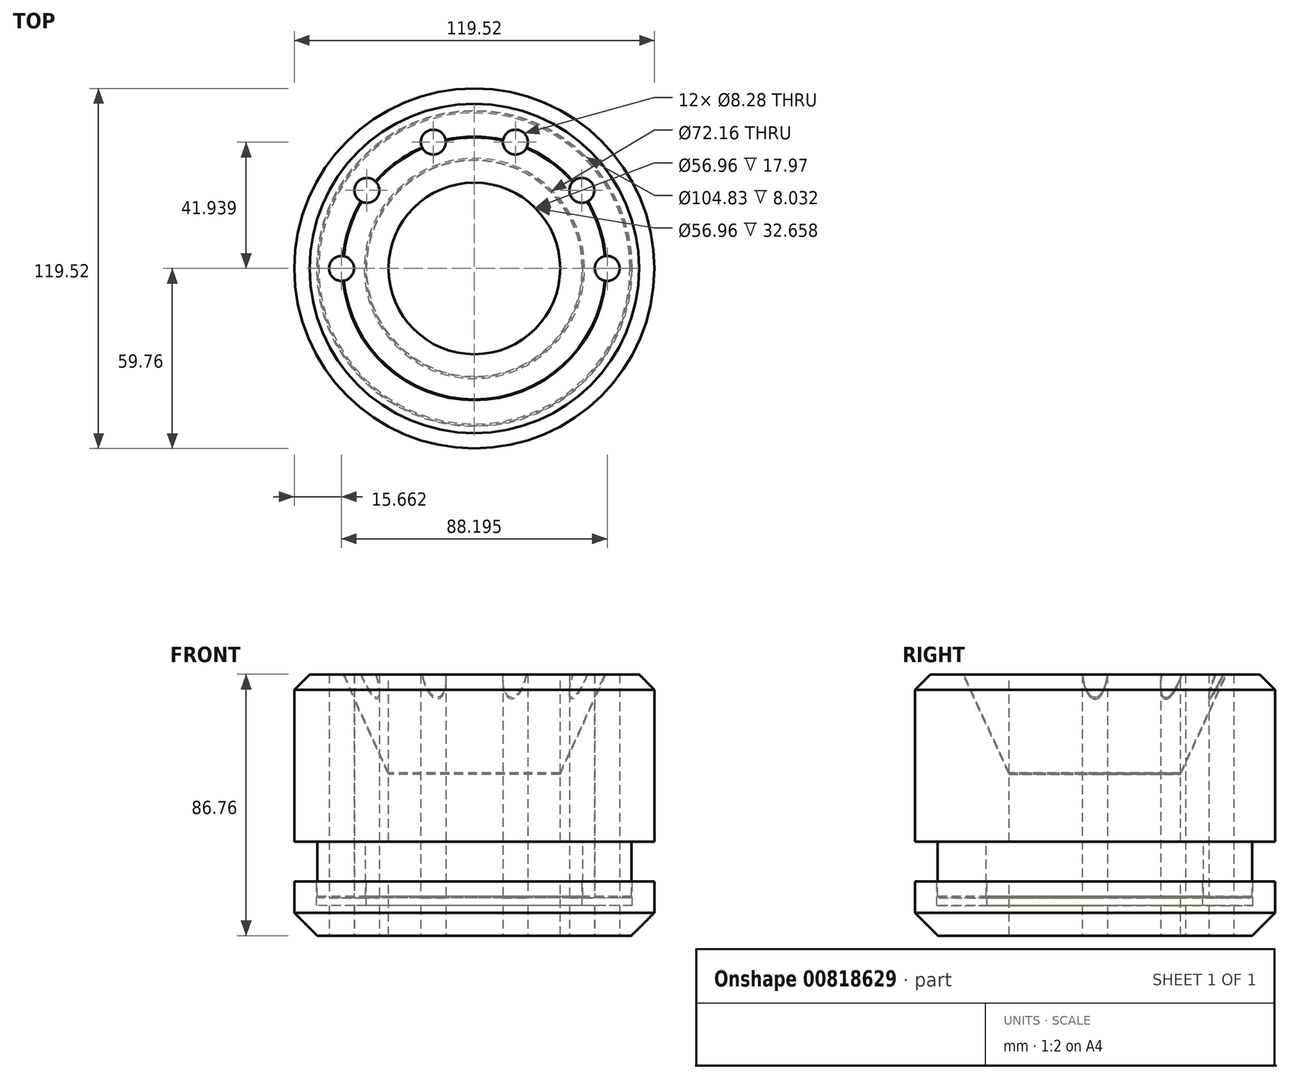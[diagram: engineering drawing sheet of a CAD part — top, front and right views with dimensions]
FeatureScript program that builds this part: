
annotation { "Feature Type Name" : "Feature", "Feature Type Description" : "" }
export const myFeature = defineFeature(function(context is Context, id is Id, definition is map)
    precondition{}
    {
        {
            var Q0;
            Q0=qCreatedBy(makeId("Front.planeOp"),FACE);
            var sketch = newSketch(context, id + "F0", { "sketchPlane" : qUnion([Q0])});
            skLineSegment(sketch, "E0.bottom", {"start": v(-28.48, 14.74) * mm, "end": v(-36.08, 14.74) * mm});
            skLineSegment(sketch, "E0.top", {"start": v(-28.48, 24.8) * mm, "end": v(-59.76, 24.8) * mm});
            skLineSegment(sketch, "E0.left", {"start": v(-28.48, 14.74) * mm, "end": v(-28.48, 24.8) * mm});
            skLineSegment(sketch, "E0.right", {"start": v(-59.76, 14.74) * mm, "end": v(-59.76, 24.8) * mm});
            skPoint(sketch, "E0.middle", {"position": v(-44.12, 19.77) * mm});
            skLineSegment(sketch, "E1.bottom", {"start": v(-36.08, -3.98) * mm, "end": v(-52.16, -3.98) * mm});
            skLineSegment(sketch, "E1.left", {"start": v(-36.08, -3.98) * mm, "end": v(-36.08, 14.74) * mm});
            skLineSegment(sketch, "E1.right", {"start": v(-52.16, -3.98) * mm, "end": v(-52.16, 14.74) * mm});
            skPoint(sketch, "E1.middle", {"position": v(-44.12, 5.33) * mm});
            skLineSegment(sketch, "E2.trimOffspring", {"start": v(-52.16, 14.74) * mm, "end": v(-59.76, 14.74) * mm});
            skLineSegment(sketch, "E3.bottom", {"start": v(-28.48, 1.52) * mm, "end": v(-35.82, 1.52) * mm});
            skLineSegment(sketch, "E3.top", {"start": v(-28.48, -16.45) * mm, "end": v(-59.76, -16.45) * mm});
            skLineSegment(sketch, "E3.left", {"start": v(-28.48, 1.52) * mm, "end": v(-28.48, -16.45) * mm});
            skLineSegment(sketch, "E3.right", {"start": v(-59.76, 1.52) * mm, "end": v(-59.76, -16.45) * mm});
            skPoint(sketch, "E3.middle", {"position": v(-44.12, -7.47) * mm});
            skPoint(sketch, "E3.middle.positionSnap0", {"position": v(-44.12, -3.98) * mm});
            skPoint(sketch, "E3.centerSnap0", {"position": v(-44.12, -3.98) * mm});
            skLineSegment(sketch, "E4.0", {"start": v(-52.41, -6.52) * mm, "end": v(-52.41, 1.52) * mm});
            skLineSegment(sketch, "E5.0", {"start": v(-35.82, -6.52) * mm, "end": v(-35.82, 1.52) * mm});
            skLineSegment(sketch, "E6.0", {"start": v(-35.82, -6.52) * mm, "end": v(-52.41, -6.52) * mm});
            skLineSegment(sketch, "E7.trimOffspring", {"start": v(-52.41, 1.52) * mm, "end": v(-59.76, 1.52) * mm});
            skLineSegment(sketch, "E8", {"start": v(0, 57.13) * mm, "end": v(0, -56.52) * mm, "construction": true});
            skLineSegment(sketch, "E9.top", {"start": v(-28.48, 70.3) * mm, "end": v(-43.48, 70.3) * mm});
            skLineSegment(sketch, "E9.left", {"start": v(-28.48, 24.8) * mm, "end": v(-28.48, 37.04) * mm});
            skLineSegment(sketch, "E9.right", {"start": v(-59.76, 24.8) * mm, "end": v(-59.76, 70.3) * mm});
            skPoint(sketch, "E9.middle", {"position": v(-44.12, 47.55) * mm});
            skLineSegment(sketch, "E10", {"start": v(-43.76, 70.3) * mm, "end": v(-28.48, 37.04) * mm});
            skLineSegment(sketch, "E11.0", {"start": v(-43.48, 70.3) * mm, "end": v(-28.48, 37.65) * mm});
            skLineSegment(sketch, "E12.trimOffspring", {"start": v(-43.76, 70.3) * mm, "end": v(-59.76, 70.3) * mm});
            skLineSegment(sketch, "E13.trimOffspring", {"start": v(-28.48, 37.65) * mm, "end": v(-28.48, 70.3) * mm});
            skSolve(sketch);
        }
        {
            var Q0;
            Q0=makeQuery(id+"F0.imprint","IMPRINT",FACE,{"disambiguationData":[TD([[makeQuery(id+"F0.imprint","IMPRINT",EDGE,{"derivedFrom":sQuery(id+"F0.wireOp",EDGE,"E0.bottom")}),-1.0]])]});
            var Q1;
            Q1=makeQuery(id+"F0.imprint","IMPRINT",FACE,{"disambiguationData":[TD([[makeQuery(id+"F0.imprint","IMPRINT",EDGE,{"derivedFrom":sQuery(id+"F0.wireOp",EDGE,"E3.bottom")}),1.0]])]});
            var Q2;
            Q2=makeQuery(id+"F0.imprint","IMPRINT",FACE,{"disambiguationData":[TD([[makeQuery(id+"F0.imprint","IMPRINT",EDGE,{"derivedFrom":sQuery(id+"F0.wireOp",EDGE,"E0.top")}),-1.0]])]});
            var Q3;
            Q3=makeQuery(id+"F0.imprint","IMPRINT",FACE,{"disambiguationData":[TD([[makeQuery(id+"F0.imprint","IMPRINT",EDGE,{"derivedFrom":sQuery(id+"F0.wireOp",EDGE,"E9.top")}),1.0]])]});
            var Q4;
            Q4=sQuery(id+"F0.wireOp",EDGE,"E8");
            revolve(context, id + "F1", {"surfaceOperationType" : NewSurfaceOperationType.NEW, "entities" : qUnion([Q0, Q1, Q2, Q3]), "axis" : qUnion([Q4]), "revolveType" : RevolveType.FULL});
        }
        {
            var Q0;
            Q0=makeQuery(id+"F1.opRevolve","SWEPT_EDGE",EDGE,{"disambiguationData":[OSD([sQuery(id+"F0.wireOp",EDGE,"E3.top"),sQuery(id+"F0.wireOp",EDGE,"E3.right")])]});
            chamfer(context, id + "F2", {"entities" : qUnion([Q0]), "width" : 7.62 * mm, "tangentPropagation" : true});
        }
        {
            var Q0;
            Q0=makeQuery(id+"F1.opRevolve","SWEPT_FACE",FACE,{"disambiguationData":[OSD([sQuery(id+"F0.wireOp",EDGE,"E3.top")])]});
            var sketch = newSketch(context, id + "F3", { "sketchPlane" : qUnion([Q0])});
            skCircle(sketch, "E14", {"center": v(0, 0) * mm, "radius": 44.1 * mm, "construction": true});
            skCircle(sketch, "E15", {"center": v(-44.1, 0) * mm, "radius": 4.14 * mm});
            skCircle(sketch, "E16.1.0", {"center": v(-35.68, -25.92) * mm, "radius": 4.14 * mm});
            skCircle(sketch, "E16.2.0", {"center": v(-13.63, -41.94) * mm, "radius": 4.14 * mm});
            skCircle(sketch, "E16.3.0", {"center": v(13.63, -41.94) * mm, "radius": 4.14 * mm});
            skCircle(sketch, "E16.4.0", {"center": v(35.68, -25.92) * mm, "radius": 4.14 * mm});
            skCircle(sketch, "E16.5.0", {"center": v(44.1, 0) * mm, "radius": 4.14 * mm});
            skLineSegment(sketch, "E16.anchor1", {"start": v(0, 0) * mm, "end": v(-44.1, 0) * mm, "construction": true});
            skLineSegment(sketch, "E16.anchor2", {"start": v(0, 0) * mm, "end": v(44.1, 0) * mm, "construction": true});
            skSolve(sketch);
        }
        {
            var Q0;
            Q0 = qSketchRegion(id + "F3", true);
            extrude(context, id + "F4", {"entities" : qUnion([Q0]), "operationType" : NewBodyOperationType.REMOVE, "endBound" : BoundingType.THROUGH_ALL, "oppositeDirection" : true, "depth" : 25.4 * mm, "offsetDistance" : 25.4 * mm});
        }
        {
            var Q0;
            Q0=makeQuery(id+"F1.opRevolve","SWEPT_FACE",FACE,{"disambiguationData":[OSD([sQuery(id+"F0.wireOp",EDGE,"E1.bottom")])]});
            var sketch = newSketch(context, id + "F5", { "sketchPlane" : qUnion([Q0])});
            skCircle(sketch, "E17", {"center": v(0, 0) * mm, "radius": 44.1 * mm, "construction": true});
            skCircle(sketch, "E18", {"center": v(-44.1, 0) * mm, "radius": 4.14 * mm});
            skCircle(sketch, "E19.1.0", {"center": v(-35.68, -25.92) * mm, "radius": 4.14 * mm});
            skCircle(sketch, "E19.2.0", {"center": v(-13.63, -41.94) * mm, "radius": 4.14 * mm});
            skCircle(sketch, "E19.3.0", {"center": v(13.63, -41.94) * mm, "radius": 4.14 * mm});
            skCircle(sketch, "E19.4.0", {"center": v(35.68, -25.92) * mm, "radius": 4.14 * mm});
            skCircle(sketch, "E19.5.0", {"center": v(44.1, 0) * mm, "radius": 4.14 * mm});
            skLineSegment(sketch, "E19.anchor1", {"start": v(0, 0) * mm, "end": v(-44.1, 0) * mm, "construction": true});
            skLineSegment(sketch, "E19.anchor2", {"start": v(0, 0) * mm, "end": v(44.1, 0) * mm, "construction": true});
            skSolve(sketch);
        }
        {
            var Q0;
            Q0 = qSketchRegion(id + "F5", true);
            extrude(context, id + "F6", {"entities" : qUnion([Q0]), "operationType" : NewBodyOperationType.REMOVE, "oppositeDirection" : true, "depth" : 19.05 * mm, "offsetDistance" : 25.4 * mm});
        }
        {
            var Q0;
            Q0=makeQuery(id+"F1.opRevolve","SWEPT_EDGE",EDGE,{"disambiguationData":[OSD([sQuery(id+"F0.wireOp",EDGE,"E1.bottom"),sQuery(id+"F0.wireOp",EDGE,"E1.right")])]});
            var Q1;
            Q1=makeQuery(id+"F6.boolean.opBoolean","COPY",EDGE,{"derivedFrom":makeQuery(id+"F6.opExtrude","CAP_EDGE",EDGE,{"disambiguationData":[OSD([sQuery(id+"F5.wireOp",EDGE,"E18")])],"isStart":true})});
            var Q2;
            Q2=makeQuery(id+"F1.opRevolve","SWEPT_EDGE",EDGE,{"disambiguationData":[OSD([sQuery(id+"F0.wireOp",EDGE,"E1.bottom"),sQuery(id+"F0.wireOp",EDGE,"E1.left")])]});
            chamfer(context, id + "F7", {"entities" : qUnion([Q0, Q1, Q2]), "width" : 0.5 * mm, "tangentPropagation" : true});
        }
        {
            var Q0;
            Q0=makeQuery(id+"F1.opRevolve","SWEPT_EDGE",EDGE,{"disambiguationData":[OSD([sQuery(id+"F0.wireOp",EDGE,"E1.right"),sQuery(id+"F0.wireOp",EDGE,"E2.trimOffspring")])]});
            var Q1;
            Q1=makeQuery(id+"F1.opRevolve","SWEPT_EDGE",EDGE,{"disambiguationData":[OSD([sQuery(id+"F0.wireOp",EDGE,"E0.bottom"),sQuery(id+"F0.wireOp",EDGE,"E1.left")])]});
            fillet(context, id + "F8", {"entities" : qUnion([Q0, Q1]), "radius" : 0.5 * mm, "tangentPropagation" : true, "allowEdgeOverflow" : false});
        }
        {
            var Q0;
            Q0=makeQuery(id+"F1.opRevolve","SWEPT_EDGE",EDGE,{"disambiguationData":[OSD([sQuery(id+"F0.wireOp",EDGE,"E9.right"),sQuery(id+"F0.wireOp",EDGE,"E12.trimOffspring")])]});
            chamfer(context, id + "F9", {"entities" : qUnion([Q0]), "width" : 5.08 * mm, "tangentPropagation" : true});
        }
    });
